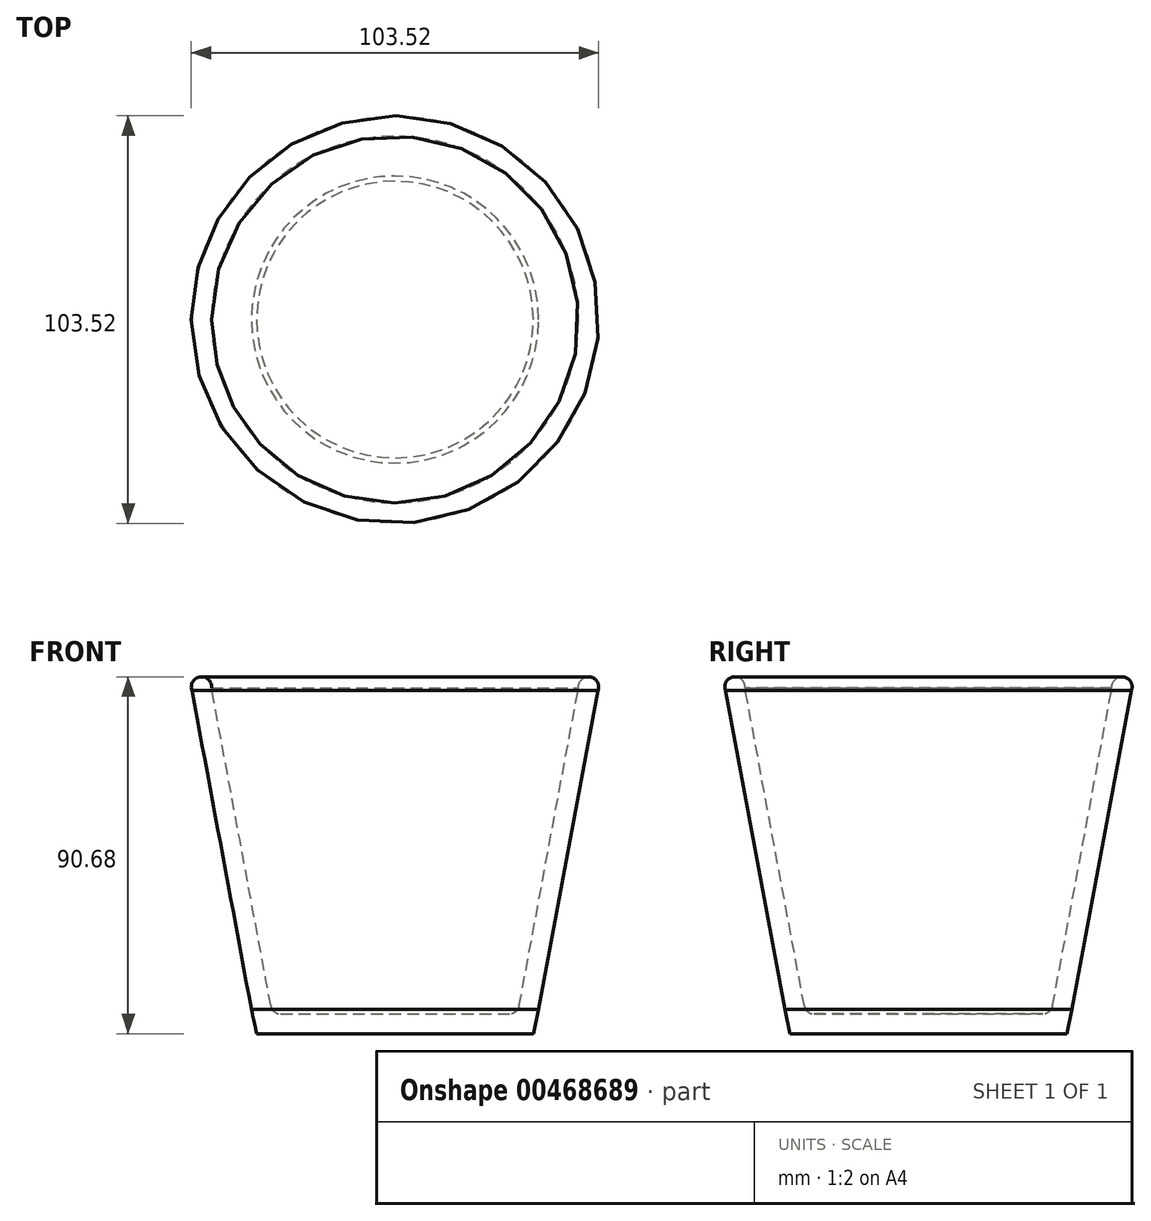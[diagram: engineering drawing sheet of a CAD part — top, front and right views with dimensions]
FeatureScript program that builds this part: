
annotation { "Feature Type Name" : "Feature", "Feature Type Description" : "" }
export const myFeature = defineFeature(function(context is Context, id is Id, definition is map)
    precondition{}
    {
        {
            var Q0;
            Q0=qCreatedBy(makeId("Front.planeOp"),FACE);
            var sketch = newSketch(context, id + "F0", { "sketchPlane" : qUnion([Q0])});
            skLineSegment(sketch, "E0", {"start": v(0, 0) * mm, "end": v(0, 86.05) * mm, "construction": true});
            skLineSegment(sketch, "E1", {"start": v(0, 0) * mm, "end": v(29.07, 0) * mm});
            skLineSegment(sketch, "E2", {"start": v(31.55, 2.06) * mm, "end": v(46.62, 82.82) * mm});
            skLineSegment(sketch, "E3", {"start": v(31.19, 0.13) * mm, "end": v(31.19, 0) * mm});
            skPoint(sketch, "E4.newPointA", {"position": v(31.19, 0) * mm});
            skPoint(sketch, "E4.newPointB", {"position": v(31.19, 0.13) * mm});
            skArc(sketch, "E4.filletArc", {"start": v(29.07, 0) * mm, "mid": v(30.68, 0.58) * mm, "end": v(31.55, 2.06) * mm});
            skLineSegment(sketch, "E5.0", {"start": v(36.46, 1.14) * mm, "end": v(51.64, 82.43) * mm});
            skLineSegment(sketch, "E6.0", {"start": v(0, -5) * mm, "end": v(29.07, -5) * mm});
            skLineSegment(sketch, "E7", {"start": v(29.07, -5) * mm, "end": v(35.14, -5) * mm});
            skLineSegment(sketch, "E8", {"start": v(35.14, -5) * mm, "end": v(36.46, 1.14) * mm});
            skLineSegment(sketch, "E9", {"start": v(0, -5) * mm, "end": v(0, 0) * mm});
            skArc(sketch, "E10", {"start": v(51.6, 82.2) * mm, "mid": v(49.5, 85.66) * mm, "end": v(46.62, 82.82) * mm});
            skSolve(sketch);
        }
        {
            var Q0;
            Q0=makeQuery(id+"F0.imprint","IMPRINT",FACE,{"disambiguationData":[TD([[makeQuery(id+"F0.imprint","IMPRINT",EDGE,{"derivedFrom":sQuery(id+"F0.wireOp",EDGE,"E1")}),-1.0]])]});
            var Q1;
            Q1=sQuery(id+"F0.wireOp",EDGE,"E9");
            revolve(context, id + "F1", {"entities" : qUnion([Q0]), "axis" : qUnion([Q1]), "revolveType" : RevolveType.FULL});
        }
    });
